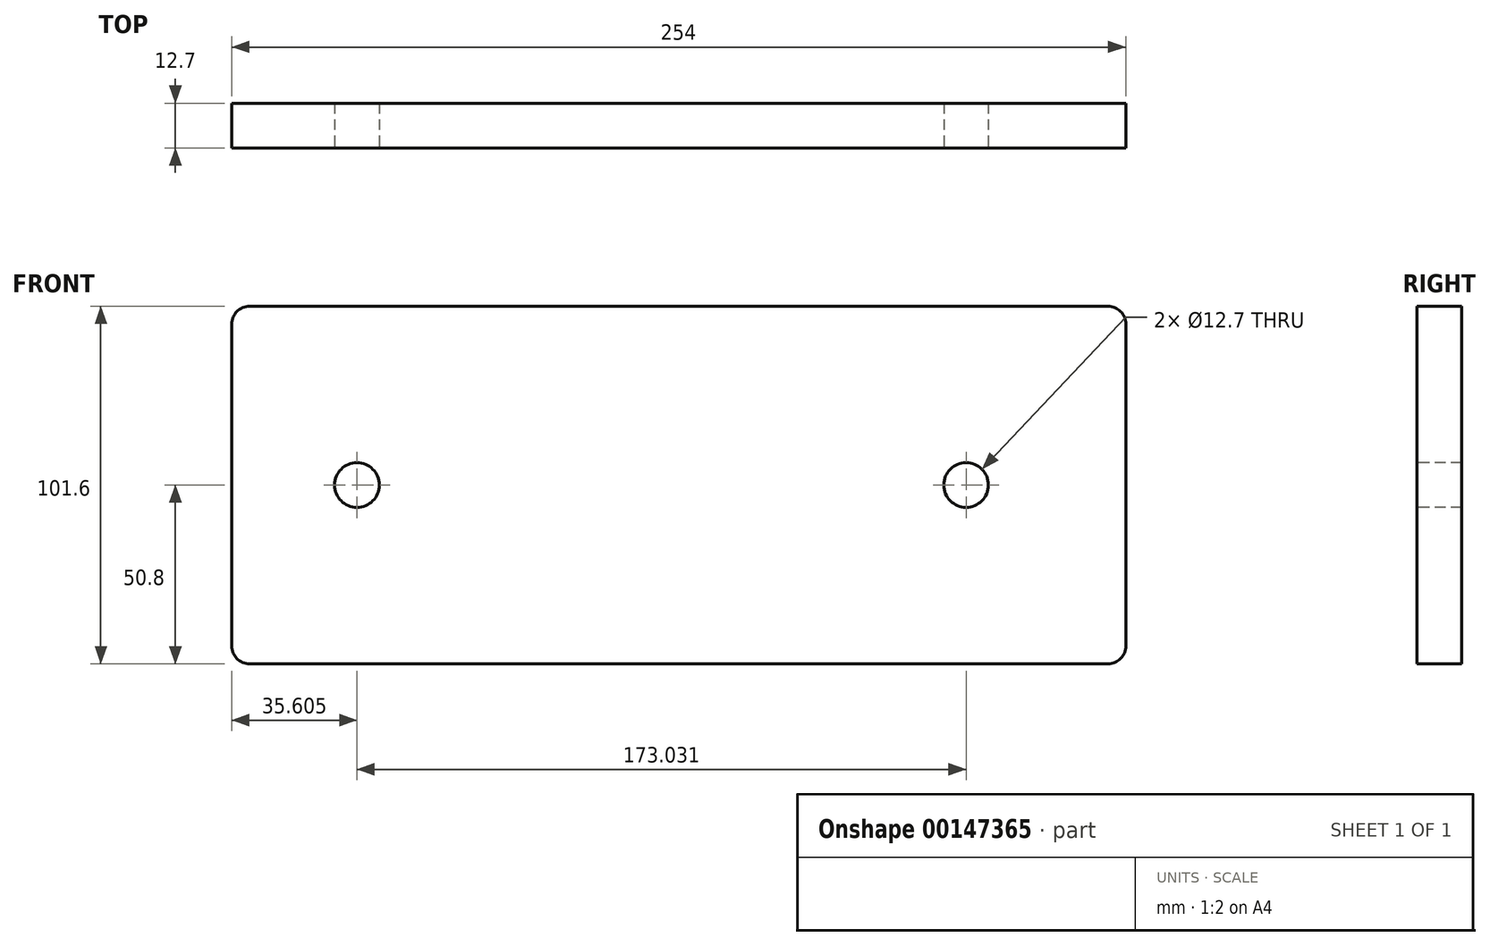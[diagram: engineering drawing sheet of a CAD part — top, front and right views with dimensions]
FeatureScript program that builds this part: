
annotation { "Feature Type Name" : "Feature", "Feature Type Description" : "" }
export const myFeature = defineFeature(function(context is Context, id is Id, definition is map)
    precondition{}
    {
        {
            var Q0;
            Q0=qCreatedBy(makeId("Front.planeOp"),FACE);
            var sketch = newSketch(context, id + "F0", { "sketchPlane" : qUnion([Q0])});
            skLineSegment(sketch, "E0.bottom", {"start": v(-89, 37.95) * mm, "end": v(165, 37.95) * mm});
            skLineSegment(sketch, "E0.top", {"start": v(-89, -63.65) * mm, "end": v(165, -63.65) * mm});
            skLineSegment(sketch, "E0.left", {"start": v(-89, 37.95) * mm, "end": v(-89, -63.65) * mm});
            skLineSegment(sketch, "E0.right", {"start": v(165, 37.95) * mm, "end": v(165, -63.65) * mm});
            skSolve(sketch);
        }
        {
            var Q0;
            Q0 = qSketchRegion(id + "F0", true);
            extrude(context, id + "F1", {"entities" : qUnion([Q0]), "depth" : 12.7 * mm});
        }
        {
            var Q0;
            Q0=makeQuery(id+"F1.opExtrude","CAP_FACE",FACE,{"disambiguationData":[OSD([sQuery(id+"F0.wireOp",EDGE,"E0.bottom"),sQuery(id+"F0.wireOp",EDGE,"E0.top"),sQuery(id+"F0.wireOp",EDGE,"E0.left"),sQuery(id+"F0.wireOp",EDGE,"E0.right")])],"isStart":false});
            var sketch = newSketch(context, id + "F2", { "sketchPlane" : qUnion([Q0])});
            skPoint(sketch, "E1", {"position": v(-53.39, -12.85) * mm});
            skPoint(sketch, "E2", {"position": v(119.65, -12.85) * mm});
            skSolve(sketch);
        }
        {
            var Q0;
            Q0=sQuery(id+"F2.wireOp",VERTEX,"E1");
            var Q1;
            Q1=sQuery(id+"F2.wireOp",VERTEX,"E2");
            var Q2;
            Q2=makeQuery(id+"F1.opExtrude","SWEPT_BODY",BODY,{"disambiguationData":[OSD([sQuery(id+"F0.wireOp",EDGE,"E0.bottom"),sQuery(id+"F0.wireOp",EDGE,"E0.top"),sQuery(id+"F0.wireOp",EDGE,"E0.left"),sQuery(id+"F0.wireOp",EDGE,"E0.right")])]});
            hole(context, id + "F3", {"style" : HoleStyle.SIMPLE, "endStyle" : HoleEndStyle.THROUGH, "holeDiameter" : 12.7 * mm, "locations" : qUnion([Q0, Q1]), "scope" : qUnion([Q2]), "isTappedThrough" : true});
        }
        {
            var Q0;
            Q0=makeQuery(id+"F1.opExtrude","SWEPT_EDGE",EDGE,{"disambiguationData":[OSD([sQuery(id+"F0.wireOp",EDGE,"E0.bottom"),sQuery(id+"F0.wireOp",EDGE,"E0.left")])]});
            fillet(context, id + "F4", {"entities" : qUnion([Q0]), "radius" : 5.08 * mm, "tangentPropagation" : true, "allowEdgeOverflow" : false});
        }
        {
            var Q0;
            Q0=makeQuery(id+"F1.opExtrude","SWEPT_EDGE",EDGE,{"disambiguationData":[OSD([sQuery(id+"F0.wireOp",EDGE,"E0.bottom"),sQuery(id+"F0.wireOp",EDGE,"E0.right")])]});
            fillet(context, id + "F5", {"entities" : qUnion([Q0]), "radius" : 5.08 * mm, "tangentPropagation" : true, "allowEdgeOverflow" : false});
        }
        {
            var Q0;
            Q0=makeQuery(id+"F1.opExtrude","SWEPT_EDGE",EDGE,{"disambiguationData":[OSD([sQuery(id+"F0.wireOp",EDGE,"E0.top"),sQuery(id+"F0.wireOp",EDGE,"E0.left")])]});
            fillet(context, id + "F6", {"entities" : qUnion([Q0]), "radius" : 5.08 * mm, "tangentPropagation" : true, "allowEdgeOverflow" : false});
        }
        {
            var Q0;
            Q0=makeQuery(id+"F1.opExtrude","SWEPT_EDGE",EDGE,{"disambiguationData":[OSD([sQuery(id+"F0.wireOp",EDGE,"E0.top"),sQuery(id+"F0.wireOp",EDGE,"E0.right")])]});
            fillet(context, id + "F7", {"entities" : qUnion([Q0]), "radius" : 5.08 * mm, "tangentPropagation" : true, "allowEdgeOverflow" : false});
        }
    });
